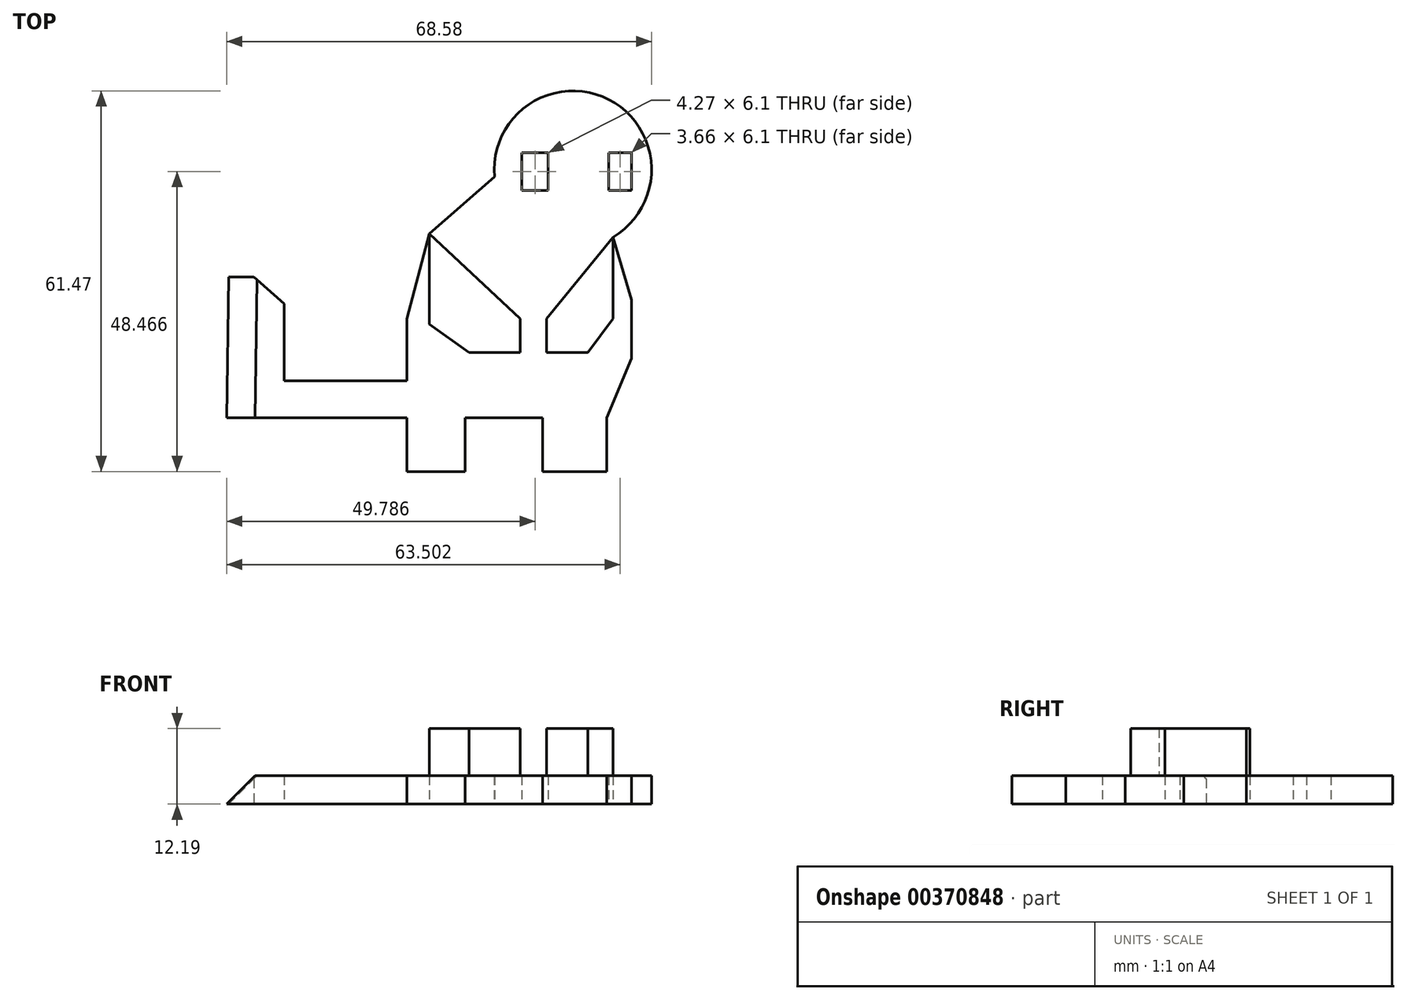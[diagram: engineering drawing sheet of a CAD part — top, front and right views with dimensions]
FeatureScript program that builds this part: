
annotation { "Feature Type Name" : "Feature", "Feature Type Description" : "" }
export const myFeature = defineFeature(function(context is Context, id is Id, definition is map)
    precondition{}
    {
        {
            var Q0;
            Q0=qCreatedBy(makeId("Top.planeOp"),FACE);
            var sketch = newSketch(context, id + "F0", { "sketchPlane" : qUnion([Q0])});
            skCircle(sketch, "E0", {"center": v(26.82, 40.08) * mm, "radius": 12.7 * mm});
            skLineSegment(sketch, "E1", {"start": v(14.18, 38.9) * mm, "end": v(3.66, 29.72) * mm});
            skLineSegment(sketch, "E2", {"start": v(3.66, 29.72) * mm, "end": v(0, 16) * mm});
            skLineSegment(sketch, "E3", {"start": v(0, 16) * mm, "end": v(0, 5.94) * mm});
            skLineSegment(sketch, "E4", {"start": v(0, 5.94) * mm, "end": v(-19.81, 5.94) * mm});
            skLineSegment(sketch, "E5", {"start": v(-29.57, 0) * mm, "end": v(0, 0) * mm});
            skLineSegment(sketch, "E6", {"start": v(0, 0) * mm, "end": v(0, 5.94) * mm});
            skLineSegment(sketch, "E7", {"start": v(0, 0) * mm, "end": v(0, -8.69) * mm});
            skLineSegment(sketch, "E8", {"start": v(0, -8.69) * mm, "end": v(9.45, -8.69) * mm});
            skLineSegment(sketch, "E9", {"start": v(9.45, -8.69) * mm, "end": v(9.45, 0) * mm});
            skLineSegment(sketch, "E10", {"start": v(9.45, 0) * mm, "end": v(21.95, 0) * mm});
            skLineSegment(sketch, "E11", {"start": v(21.95, 0) * mm, "end": v(21.95, -8.69) * mm});
            skLineSegment(sketch, "E12", {"start": v(21.95, -8.69) * mm, "end": v(32.3, -8.69) * mm});
            skLineSegment(sketch, "E13", {"start": v(32.3, -8.69) * mm, "end": v(32.3, 0) * mm});
            skLineSegment(sketch, "E14", {"start": v(32.3, 0) * mm, "end": v(36.27, 9.6) * mm});
            skLineSegment(sketch, "E15", {"start": v(36.27, 9.6) * mm, "end": v(36.27, 19.05) * mm});
            skLineSegment(sketch, "E16", {"start": v(3.66, 29.72) * mm, "end": v(3.66, 15.7) * mm});
            skLineSegment(sketch, "E17", {"start": v(3.66, 15.7) * mm, "end": v(11.89, 9.9) * mm});
            skLineSegment(sketch, "E18", {"start": v(19.2, 9.9) * mm, "end": v(11.89, 9.9) * mm});
            skLineSegment(sketch, "E19", {"start": v(19.2, 9.9) * mm, "end": v(19.2, 15.7) * mm});
            skLineSegment(sketch, "E20", {"start": v(3.66, 29.72) * mm, "end": v(19.2, 15.7) * mm});
            skPoint(sketch, "E21.endSnap0", {"position": v(36.27, 14.33) * mm});
            skLineSegment(sketch, "E22", {"start": v(32.61, 14.33) * mm, "end": v(28.04, 9.6) * mm});
            skLineSegment(sketch, "E23", {"start": v(28.04, 9.6) * mm, "end": v(23.77, 9.6) * mm});
            skLineSegment(sketch, "E24", {"start": v(23.77, 9.6) * mm, "end": v(23.77, 14.33) * mm});
            skLineSegment(sketch, "E25", {"start": v(18.6, 42.82) * mm, "end": v(18.6, 36.73) * mm});
            skLineSegment(sketch, "E26", {"start": v(18.6, 36.73) * mm, "end": v(22.86, 36.73) * mm});
            skLineSegment(sketch, "E27", {"start": v(18.6, 42.82) * mm, "end": v(22.86, 42.82) * mm});
            skLineSegment(sketch, "E28", {"start": v(22.86, 42.82) * mm, "end": v(22.86, 36.73) * mm});
            skLineSegment(sketch, "E29", {"start": v(32.61, 42.82) * mm, "end": v(32.61, 36.73) * mm});
            skLineSegment(sketch, "E30", {"start": v(32.61, 36.73) * mm, "end": v(36.27, 36.73) * mm});
            skLineSegment(sketch, "E31", {"start": v(36.27, 36.73) * mm, "end": v(36.27, 42.82) * mm});
            skLineSegment(sketch, "E32", {"start": v(36.27, 42.82) * mm, "end": v(32.61, 42.82) * mm});
            skLineSegment(sketch, "E33", {"start": v(-19.81, 5.94) * mm, "end": v(-19.81, 18.44) * mm});
            skLineSegment(sketch, "E34", {"start": v(-19.81, 18.44) * mm, "end": v(-24.69, 22.7) * mm});
            skLineSegment(sketch, "E35", {"start": v(-24.69, 22.7) * mm, "end": v(-29.26, 22.7) * mm});
            skLineSegment(sketch, "E36", {"start": v(-29.26, 22.7) * mm, "end": v(-29.57, 0) * mm});
            skLineSegment(sketch, "E37", {"start": v(36.27, 19.05) * mm, "end": v(33.28, 29.15) * mm});
            skLineSegment(sketch, "E38", {"start": v(32.61, 14.33) * mm, "end": v(33.28, 29.15) * mm});
            skLineSegment(sketch, "E39", {"start": v(23.77, 14.33) * mm, "end": v(33.28, 29.15) * mm});
            skSolve(sketch);
        }
        {
            var Q0;
            Q0=makeQuery(id+"F0.imprint","IMPRINT",FACE,{"disambiguationData":[TD([[makeQuery(id+"F0.imprint","IMPRINT",EDGE,{"derivedFrom":sQuery(id+"F0.wireOp",EDGE,"E4")}),1.0]])]});
            var Q1;
            Q1=makeQuery(id+"F0.imprint","IMPRINT",FACE,{"disambiguationData":[TD([[makeQuery(id+"F0.imprint","IMPRINT",EDGE,{"derivedFrom":sQuery(id+"F0.wireOp",EDGE,"E25")}),-1.0]])]});
            var Q2;
            {var subQ0=sQuery(id+"F0.wireOp",EDGE,"E1");Q2=makeQuery(id+"F0.imprint","IMPRINT",FACE,{"disambiguationData":[TD([[makeQuery(id+"F0.imprint","IMPRINT",EDGE,{"derivedFrom":subQ0}),1.0]])]});}
            var Q3;
            Q3=makeQuery(id+"F0.imprint","IMPRINT",FACE,{"disambiguationData":[TD([[makeQuery(id+"F0.imprint","IMPRINT",EDGE,{"derivedFrom":sQuery(id+"F0.wireOp",EDGE,"E16")}),1.0]])]});
            var Q4;
            Q4=makeQuery(id+"F0.imprint","IMPRINT",FACE,{"disambiguationData":[TD([[makeQuery(id+"F0.imprint","IMPRINT",EDGE,{"derivedFrom":sQuery(id+"F0.wireOp",EDGE,"E22")}),-1.0]])]});
            extrude(context, id + "F1", {"entities" : qUnion([Q0, Q1, Q2, Q3, Q4]), "depth" : 4.57 * mm});
        }
        {
            var Q0;
            Q0=makeQuery(id+"F1.opExtrude","CAP_FACE",FACE,{"disambiguationData":[OSD([sQuery(id+"F0.wireOp",EDGE,"E0"),sQuery(id+"F0.wireOp",EDGE,"E1"),sQuery(id+"F0.wireOp",EDGE,"E2"),sQuery(id+"F0.wireOp",EDGE,"E3"),sQuery(id+"F0.wireOp",EDGE,"E4"),sQuery(id+"F0.wireOp",EDGE,"E5"),sQuery(id+"F0.wireOp",EDGE,"E7"),sQuery(id+"F0.wireOp",EDGE,"E8"),sQuery(id+"F0.wireOp",EDGE,"E9"),sQuery(id+"F0.wireOp",EDGE,"E10"),sQuery(id+"F0.wireOp",EDGE,"E11"),sQuery(id+"F0.wireOp",EDGE,"E12"),sQuery(id+"F0.wireOp",EDGE,"E13"),sQuery(id+"F0.wireOp",EDGE,"E14"),sQuery(id+"F0.wireOp",EDGE,"E15"),sQuery(id+"F0.wireOp",EDGE,"E25"),sQuery(id+"F0.wireOp",EDGE,"E26"),sQuery(id+"F0.wireOp",EDGE,"E27"),sQuery(id+"F0.wireOp",EDGE,"E28"),sQuery(id+"F0.wireOp",EDGE,"E29"),sQuery(id+"F0.wireOp",EDGE,"E30"),sQuery(id+"F0.wireOp",EDGE,"E31"),sQuery(id+"F0.wireOp",EDGE,"E32"),sQuery(id+"F0.wireOp",EDGE,"E33"),sQuery(id+"F0.wireOp",EDGE,"E34"),sQuery(id+"F0.wireOp",EDGE,"E35"),sQuery(id+"F0.wireOp",EDGE,"E36"),sQuery(id+"F0.wireOp",EDGE,"E37")])],"isStart":false});
            var sketch = newSketch(context, id + "F2", { "sketchPlane" : qUnion([Q0])});
            skLineSegment(sketch, "E40", {"start": v(3.66, 29.72) * mm, "end": v(3.66, 15.09) * mm});
            skLineSegment(sketch, "E41", {"start": v(3.66, 15.09) * mm, "end": v(10.06, 10.52) * mm});
            skLineSegment(sketch, "E42", {"start": v(10.06, 10.52) * mm, "end": v(18.29, 10.52) * mm});
            skLineSegment(sketch, "E43", {"start": v(18.29, 10.52) * mm, "end": v(18.29, 16) * mm});
            skLineSegment(sketch, "E44", {"start": v(18.29, 16) * mm, "end": v(3.66, 29.72) * mm});
            skLineSegment(sketch, "E45", {"start": v(33.28, 29.15) * mm, "end": v(33.28, 16) * mm});
            skLineSegment(sketch, "E46", {"start": v(33.28, 16) * mm, "end": v(29.26, 10.52) * mm});
            skLineSegment(sketch, "E47", {"start": v(29.26, 10.52) * mm, "end": v(22.56, 10.52) * mm});
            skLineSegment(sketch, "E48", {"start": v(22.56, 10.52) * mm, "end": v(22.56, 16) * mm});
            skLineSegment(sketch, "E49", {"start": v(22.56, 16) * mm, "end": v(33.28, 29.15) * mm});
            skSolve(sketch);
        }
        {
            var Q0;
            Q0=makeQuery(id+"F2.imprint","IMPRINT",FACE,{"disambiguationData":[TD([[makeQuery(id+"F2.imprint","IMPRINT",EDGE,{"derivedFrom":sQuery(id+"F2.wireOp",EDGE,"E40")}),1.0]])]});
            var Q1;
            Q1=makeQuery(id+"F2.imprint","IMPRINT",FACE,{"disambiguationData":[TD([[makeQuery(id+"F2.imprint","IMPRINT",EDGE,{"derivedFrom":sQuery(id+"F2.wireOp",EDGE,"E45")}),-1.0]])]});
            extrude(context, id + "F3", {"entities" : qUnion([Q0, Q1]), "operationType" : NewBodyOperationType.ADD, "depth" : 7.62 * mm});
        }
        {
            var Q0;
            Q0=makeQuery(id+"F1.opExtrude","CAP_EDGE",EDGE,{"disambiguationData":[OSD([sQuery(id+"F0.wireOp",EDGE,"E36")])],"isStart":false});
            chamfer(context, id + "F4", {"entities" : qUnion([Q0]), "width" : 5.08 * mm, "tangentPropagation" : true});
        }
    });
